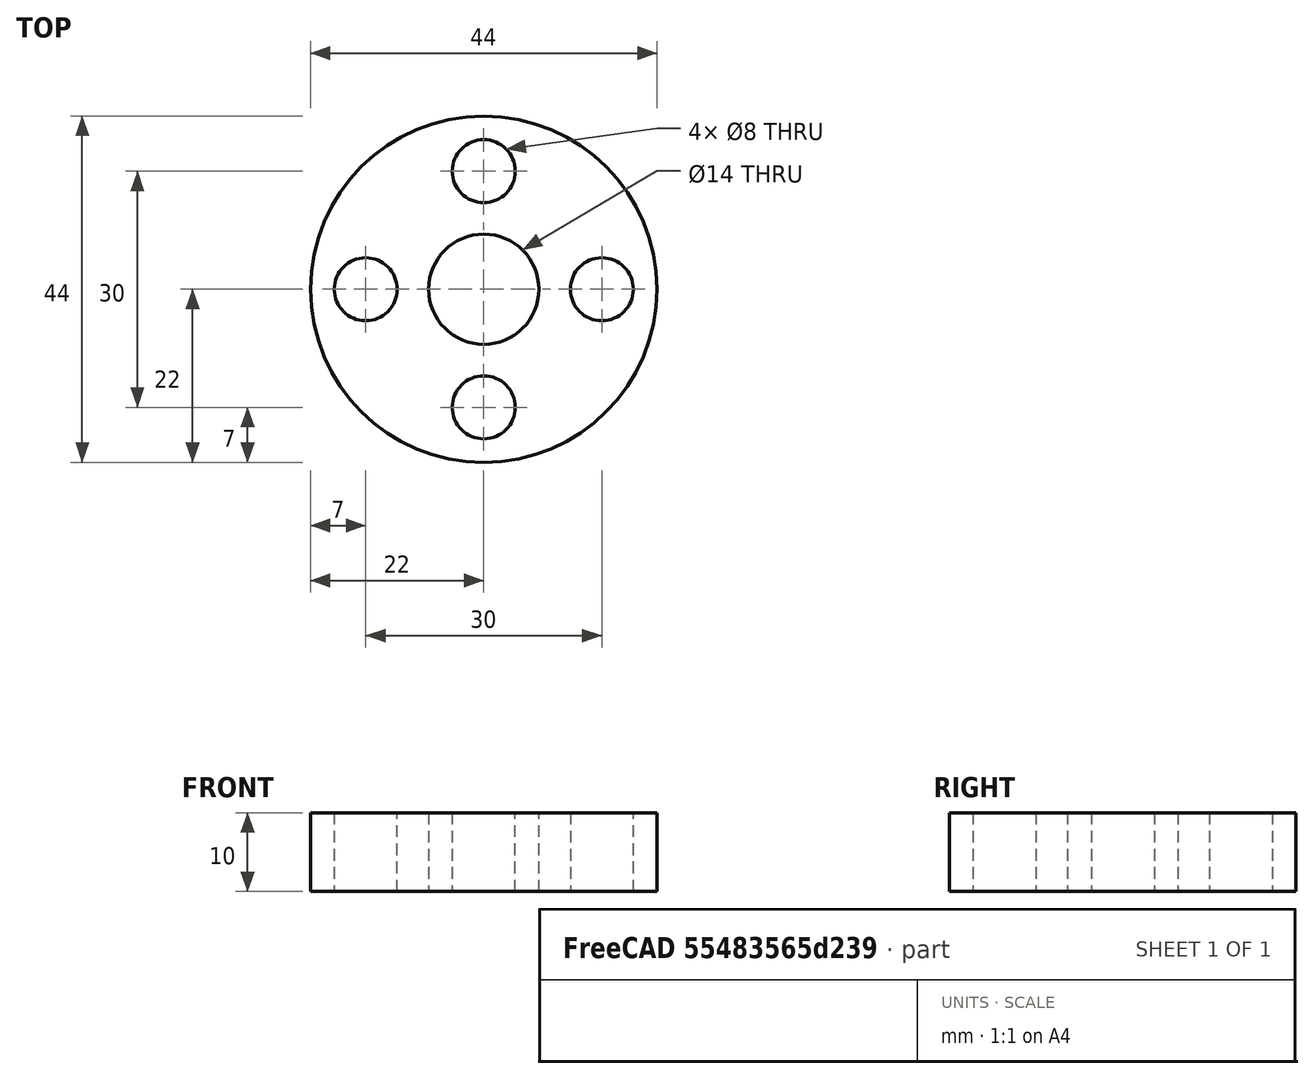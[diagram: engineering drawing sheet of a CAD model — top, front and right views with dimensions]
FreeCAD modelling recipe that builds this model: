
FCSTD DOCUMENT  (FreeCAD 0.18.4R)
Label: нижний_фанец
License: All rights reserved
LicenseURL: http://en.wikipedia.org/wiki/All_rights_reserved
objects: Sketcher::SketchObject×1, PartDesign::Pad×1, PartDesign::Body×1
note: 4 computed .brp shape members not serialized (recipe doc carries the construction recipe); baked Part::Feature solids carry a one-line shape summary decoded from their .brp

FEATURE [Sketcher::SketchObject] Sketch
  MapMode = 5
  Support = -> [XY_Plane]
  sketch-geometry (6):
    g0: Circle CenterX=0 CenterY=0 CenterZ=0 NormalX=0 NormalY=0 NormalZ=1 AngleXU=0 Radius=22
    g1: Circle CenterX=0 CenterY=15 CenterZ=0 NormalX=0 NormalY=0 NormalZ=1 AngleXU=0 Radius=4
    g2: Circle CenterX=-15 CenterY=0 CenterZ=0 NormalX=0 NormalY=0 NormalZ=1 AngleXU=0 Radius=4
    g3: Circle CenterX=15 CenterY=0 CenterZ=0 NormalX=0 NormalY=0 NormalZ=1 AngleXU=0 Radius=4
    g4: Circle CenterX=0 CenterY=-15 CenterZ=0 NormalX=0 NormalY=0 NormalZ=1 AngleXU=0 Radius=4
    g5: Circle CenterX=7e-16 CenterY=-1e-16 CenterZ=0 NormalX=0 NormalY=0 NormalZ=1 AngleXU=0 Radius=7
  constraints (17):
    c: Coincident(g0,g-1)
    c: Diameter(g0) = 44
    c: PointOnObject(g1,g-2)
    c: PointOnObject(g2,g-1)
    c: PointOnObject(g3,g-1)
    c: PointOnObject(g4,g-2)
    c: Diameter(g2) = 8
    c: Equal(g2,g1)
    c: Equal(g2,g4)
    c: Equal(g2,g3)
    c: Distance(g2,g0) = 15
    c: Distance(g1,g0) = 15
    c: Distance(g2,g3) = 30
    c: Distance(g1,g4) = 30
    c: Diameter(g5) = 14
    c: Distance(g5,g3) = 15
    c: Distance(g4,g5) = 15
FEATURE [PartDesign::Pad] Pad
  Length = 10
  Length2 = 100
  Profile = -> Sketch
  Type = 0
FEATURE [PartDesign::Body] Body
  Group = -> [Sketch,Pad]
  Origin = -> Origin
  Tip = -> Pad
